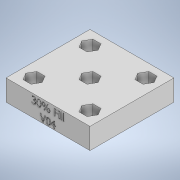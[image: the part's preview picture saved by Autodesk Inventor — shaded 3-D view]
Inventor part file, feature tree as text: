
AUTODESK INVENTOR PART (.ipt)
format: ipt  version: 2021.1 (Build 251245010, 245A)  size: 318,464 bytes
history: native  units: in
note: dims shown in document units (in); Inventor stores cm internally (conversion verified against a paired STEP export)
features: extrude x4, sketch x4, pattern_linear x1
ambient origin geometry x8: Origin, YZ Plane, XZ Plane, XY Plane, X Axis, Y Axis, Z Axis, Center Point
bodies: Solid1 (feature_tree)
feature tree (9):
  extrude  "Extrusion1"  Depth=0.75in TaperAngle=0.0deg
  extrude  "Extrusion3"  Depth=2.0in
  extrude  "Extrusion2"  Depth=0.5in
  pattern_linear  "Rectangular Pattern1"  Spacing1=0.5in  [1 undecoded]
  extrude  "Extrusion4"  Depth=0.5in
  sketch  "Sketch1"  dims[d0=3.0in d1=0.75in d2=0.0in]
  sketch  "Sketch2"  dims[d6=0.0in d7=0.0in d8=0.7874in d10=2.0in d11=0.7874in d13=2.0in]
  sketch  "Sketch3"  dims[d14=0.05in d15=0.0in d16=0.5in]
  sketch  "Sketch4"  dims[d17=0.5in d18=0.5in d19=0.5in d20=0.0in d21=0.0in]
note: 1 required parameter value undecoded (feature->parameter linkage not recoverable at this tier; creation-order binding heuristic only, values carry confidence <= 0.55)
